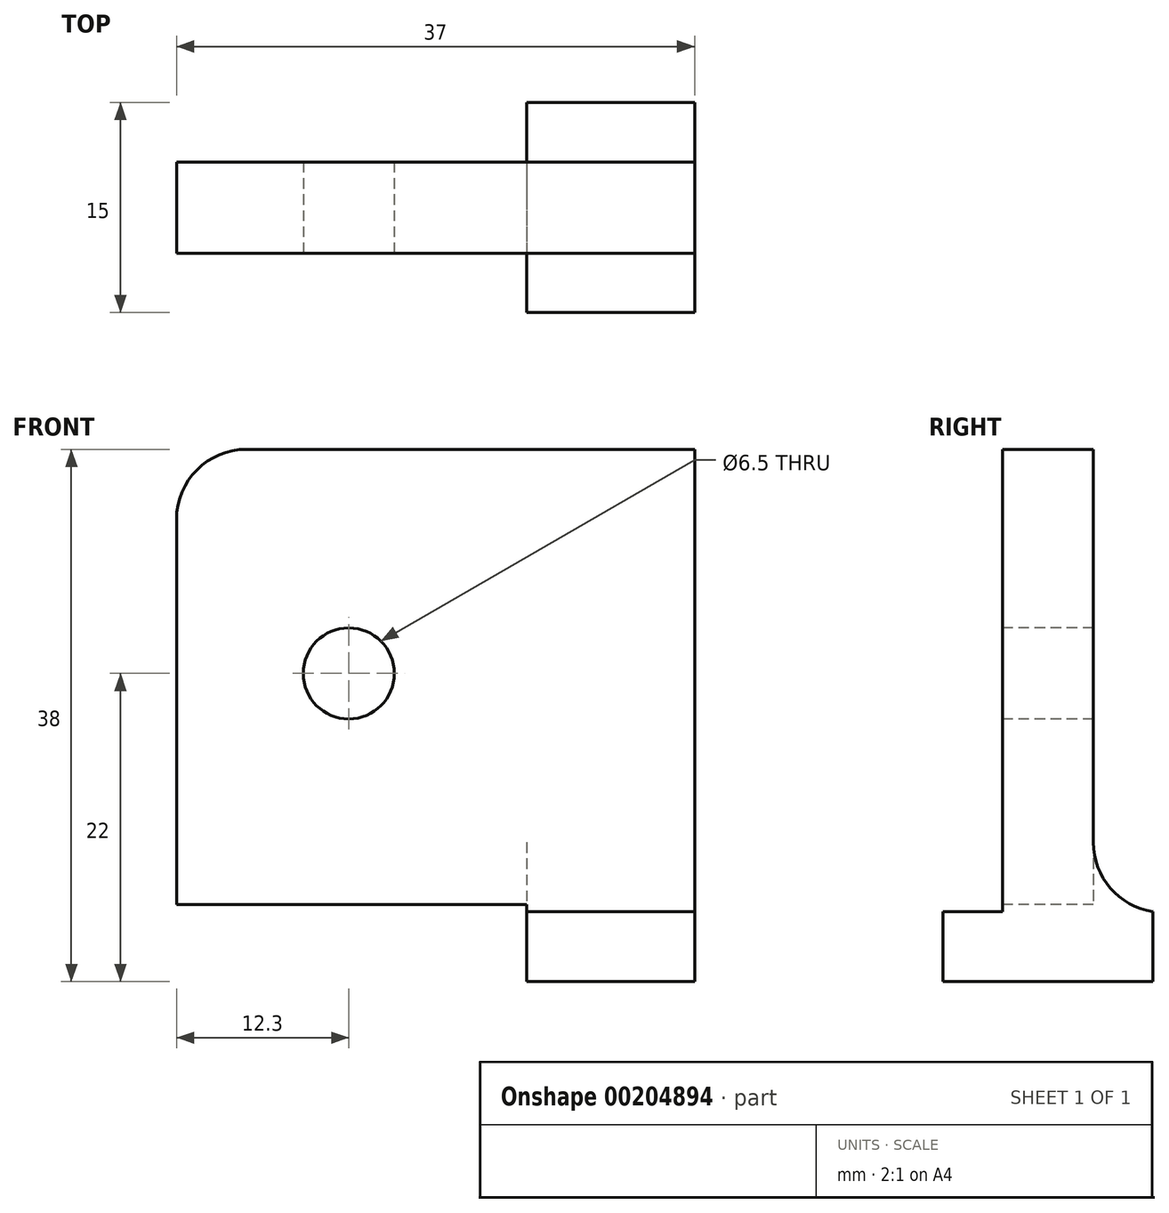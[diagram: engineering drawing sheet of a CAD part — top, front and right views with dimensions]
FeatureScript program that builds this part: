
annotation { "Feature Type Name" : "Feature", "Feature Type Description" : "" }
export const myFeature = defineFeature(function(context is Context, id is Id, definition is map)
    precondition{}
    {
        {
            var Q0;
            Q0=qCreatedBy(makeId("Top.planeOp"),FACE);
            var sketch = newSketch(context, id + "F0", { "sketchPlane" : qUnion([Q0])});
            skLineSegment(sketch, "E0.bottom", {"start": v(-6, 7.5) * mm, "end": v(6, 7.5) * mm});
            skLineSegment(sketch, "E0.top", {"start": v(-6, -7.5) * mm, "end": v(6, -7.5) * mm});
            skLineSegment(sketch, "E0.left", {"start": v(-6, 7.5) * mm, "end": v(-6, -7.5) * mm});
            skLineSegment(sketch, "E0.right", {"start": v(6, 7.5) * mm, "end": v(6, -7.5) * mm});
            skSolve(sketch);
        }
        {
            var Q0;
            Q0 = qSketchRegion(id + "F0", true);
            extrude(context, id + "F1", {"entities" : qUnion([Q0]), "depth" : 5 * mm});
        }
        {
            var Q0;
            Q0=makeQuery(id+"F1.opExtrude","CAP_FACE",FACE,{"disambiguationData":[OSD([sQuery(id+"F0.wireOp",EDGE,"E0.bottom"),sQuery(id+"F0.wireOp",EDGE,"E0.top"),sQuery(id+"F0.wireOp",EDGE,"E0.left"),sQuery(id+"F0.wireOp",EDGE,"E0.right")])],"isStart":false});
            var sketch = newSketch(context, id + "F2", { "sketchPlane" : qUnion([Q0])});
            skLineSegment(sketch, "E1.bottom", {"start": v(-6, 3.25) * mm, "end": v(6, 3.25) * mm});
            skLineSegment(sketch, "E1.top", {"start": v(-6, -3.25) * mm, "end": v(6, -3.25) * mm});
            skLineSegment(sketch, "E1.left", {"start": v(-6, 3.25) * mm, "end": v(-6, -3.25) * mm});
            skLineSegment(sketch, "E1.right", {"start": v(6, 3.25) * mm, "end": v(6, -3.25) * mm});
            skSolve(sketch);
        }
        {
            var Q0;
            Q0 = qSketchRegion(id + "F2", true);
            extrude(context, id + "F3", {"entities" : qUnion([Q0]), "operationType" : NewBodyOperationType.ADD, "depth" : 33 * mm});
        }
        {
            var Q0;
            Q0=makeQuery(id+"F3.boolean.opBoolean","MERGE",FACE,{"derivedFrom":[makeQuery(id+"F1.opExtrude","SWEPT_FACE",FACE,{"disambiguationData":[OSD([sQuery(id+"F0.wireOp",EDGE,"E0.left")])]}),makeQuery(id+"F3.opExtrude","SWEPT_FACE",FACE,{"disambiguationData":[OSD([sQuery(id+"F2.wireOp",EDGE,"E1.left")])]})]});
            var sketch = newSketch(context, id + "F4", { "sketchPlane" : qUnion([Q0])});
            skLineSegment(sketch, "E2.bottom", {"start": v(-3.25, 38) * mm, "end": v(3.25, 38) * mm});
            skLineSegment(sketch, "E2.top", {"start": v(-3.25, 5) * mm, "end": v(3.25, 5) * mm});
            skLineSegment(sketch, "E2.left", {"start": v(-3.25, 38) * mm, "end": v(-3.25, 5) * mm});
            skLineSegment(sketch, "E2.right", {"start": v(3.25, 38) * mm, "end": v(3.25, 5) * mm});
            skSolve(sketch);
        }
        {
            var Q0;
            Q0 = qSketchRegion(id + "F4", true);
            extrude(context, id + "F5", {"entities" : qUnion([Q0]), "operationType" : NewBodyOperationType.ADD, "depth" : 25 * mm});
        }
        {
            var Q0;
            Q0=makeQuery(id+"F3.opExtrude","CAP_EDGE",EDGE,{"disambiguationData":[OSD([sQuery(id+"F2.wireOp",EDGE,"E1.top")])],"isStart":true});
            var Q1;
            Q1=makeQuery(id+"F3.opExtrude","CAP_EDGE",EDGE,{"disambiguationData":[OSD([sQuery(id+"F2.wireOp",EDGE,"E1.bottom")])],"isStart":true});
            fillet(context, id + "F6", {"entities" : qUnion([Q0, Q1]), "radius" : 5 * mm, "tangentPropagation" : true, "allowEdgeOverflow" : false});
        }
        {
            var Q0;
            Q0=makeQuery(id+"F5.boolean.opBoolean","MERGE",FACE,{"derivedFrom":[makeQuery(id+"F3.opExtrude","SWEPT_FACE",FACE,{"disambiguationData":[OSD([sQuery(id+"F2.wireOp",EDGE,"E1.top")])]}),makeQuery(id+"F5.opExtrude","SWEPT_FACE",FACE,{"disambiguationData":[OSD([sQuery(id+"F4.wireOp",EDGE,"E2.right")])]})]});
            var sketch = newSketch(context, id + "F7", { "sketchPlane" : qUnion([Q0])});
            skLineSegment(sketch, "E3", {"start": v(-6, 9.94) * mm, "end": v(-6, 37) * mm});
            skCircle(sketch, "E4", {"center": v(-18.7, 22) * mm, "radius": 3.25 * mm});
            skSolve(sketch);
        }
        {
            var Q0;
            Q0 = qSketchRegion(id + "F7", true);
            extrude(context, id + "F8", {"entities" : qUnion([Q0]), "operationType" : NewBodyOperationType.REMOVE, "oppositeDirection" : true, "depth" : 25 * mm});
        }
        {
            var Q0;
            Q0=makeQuery(id+"F5.opExtrude","CAP_FACE",FACE,{"disambiguationData":[OSD([sQuery(id+"F4.wireOp",EDGE,"E2.bottom"),sQuery(id+"F4.wireOp",EDGE,"E2.top"),sQuery(id+"F4.wireOp",EDGE,"E2.left"),sQuery(id+"F4.wireOp",EDGE,"E2.right")])],"isStart":false});
            var sketch = newSketch(context, id + "F9", { "sketchPlane" : qUnion([Q0])});
            skLineSegment(sketch, "E5.bottom", {"start": v(-3.25, 5) * mm, "end": v(3.25, 5) * mm});
            skLineSegment(sketch, "E5.top", {"start": v(-3.25, 5.5) * mm, "end": v(3.25, 5.5) * mm});
            skLineSegment(sketch, "E5.left", {"start": v(-3.25, 5) * mm, "end": v(-3.25, 5.5) * mm});
            skLineSegment(sketch, "E5.right", {"start": v(3.25, 5) * mm, "end": v(3.25, 5.5) * mm});
            skSolve(sketch);
        }
        {
            var Q0;
            Q0 = qSketchRegion(id + "F9", true);
            extrude(context, id + "F10", {"entities" : qUnion([Q0]), "operationType" : NewBodyOperationType.REMOVE, "oppositeDirection" : true, "depth" : 25 * mm});
        }
        {
            var Q0;
            Q0=makeQuery(id+"F5.opExtrude","CAP_EDGE",EDGE,{"disambiguationData":[OSD([sQuery(id+"F4.wireOp",EDGE,"E2.bottom")])],"isStart":false});
            fillet(context, id + "F11", {"entities" : qUnion([Q0]), "radius" : 5 * mm, "tangentPropagation" : true, "allowEdgeOverflow" : false});
        }
    });
